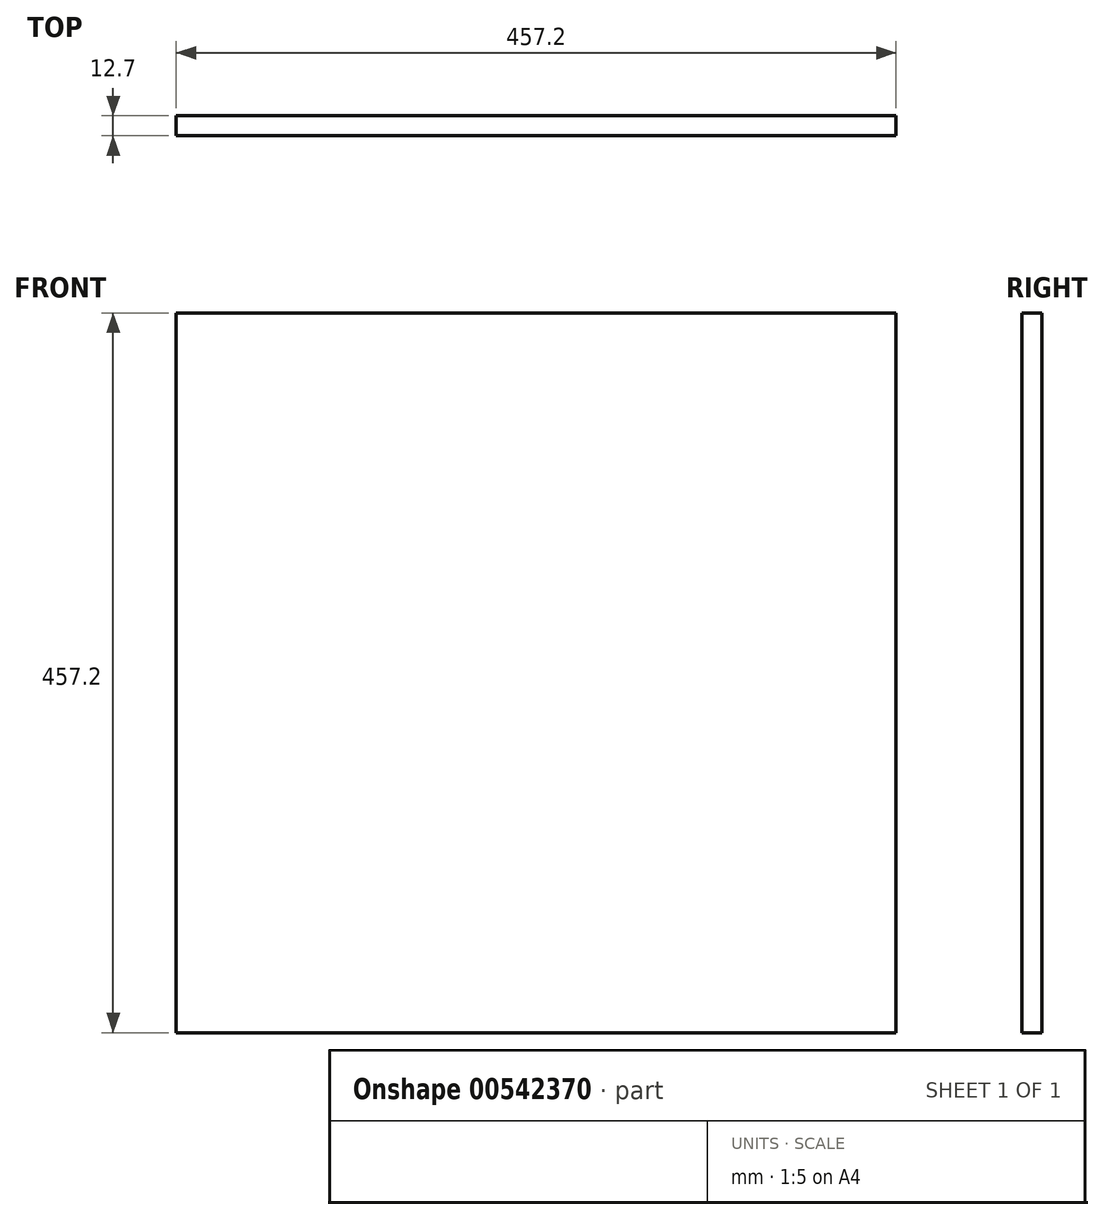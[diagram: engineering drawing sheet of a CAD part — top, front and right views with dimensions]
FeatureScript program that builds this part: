
annotation { "Feature Type Name" : "Feature", "Feature Type Description" : "" }
export const myFeature = defineFeature(function(context is Context, id is Id, definition is map)
    precondition{}
    {
        {
            var Q0;
            Q0=qCreatedBy(makeId("Front.planeOp"),FACE);
            var sketch = newSketch(context, id + "F0", { "sketchPlane" : qUnion([Q0])});
            skLineSegment(sketch, "E0.bottom", {"start": v(228.6, -228.6) * mm, "end": v(-228.6, -228.6) * mm});
            skLineSegment(sketch, "E0.top", {"start": v(228.6, 228.6) * mm, "end": v(-228.6, 228.6) * mm});
            skLineSegment(sketch, "E0.left", {"start": v(228.6, -228.6) * mm, "end": v(228.6, 228.6) * mm});
            skLineSegment(sketch, "E0.right", {"start": v(-228.6, -228.6) * mm, "end": v(-228.6, 228.6) * mm});
            skPoint(sketch, "E0.middle", {"position": v(0, 0) * mm});
            skSolve(sketch);
        }
        {
            var Q0;
            Q0=makeQuery(id+"F0.imprint","IMPRINT",FACE,{"disambiguationData":[TD([[makeQuery(id+"F0.imprint","IMPRINT",EDGE,{"derivedFrom":sQuery(id+"F0.wireOp",EDGE,"E0.bottom")}),-1.0]])]});
            extrude(context, id + "F1", {"entities" : qUnion([Q0]), "depth" : 12.7 * mm, "offsetDistance" : 25.4 * mm});
        }
    });
